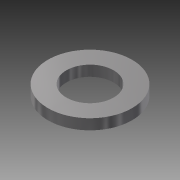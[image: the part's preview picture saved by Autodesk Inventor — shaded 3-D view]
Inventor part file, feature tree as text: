
AUTODESK INVENTOR PART (.ipt)
format: ipt  version: 2013 (Build 170138000, 138)  size: 81,408 bytes
history: native  units: mm
features: other x1, extrude x1, sketch x1
ambient origin geometry x1: Origin
feature tree (3):
  other  "ソリッド1"
  extrude  "押し出し1"  Depth=4.5mm
  sketch  "スケッチ1"
